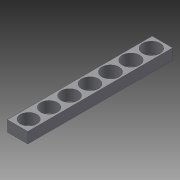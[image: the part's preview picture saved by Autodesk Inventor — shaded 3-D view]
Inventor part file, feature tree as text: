
AUTODESK INVENTOR PART (.ipt)
format: ipt  version: 2015 (Build 190159000, 159)  size: 107,008 bytes
history: native  units: in
note: dims shown in document units (in); Inventor stores cm internally (conversion verified against a paired STEP export)
features: extrude x2, sketch x2
ambient origin geometry x8: Origin, YZ Plane, XZ Plane, XY Plane, X Axis, Y Axis, Z Axis, Center Point
bodies: Solid1 (feature_tree)
feature tree (4):
  extrude  "Extrusion1"  Depth=3.3465in
  extrude  "Extrusion2"  Depth=0.4724in
  sketch  "Sketch1"  dims[d6=0.4724in d7=3.3465in]
  sketch  "Sketch2"  dims[d8=0.25in d9=0.0in d10=0.3819in d11=0.3858in d12=0.3898in d13=0.3937in d14=0.3976in d15=0.4016in d16=0.4724in d17=0.4724in d18=0.4724in d19=0.4724in d20=0.4724in d21=0.4055in d22=0.4724in d23=0.0in d24=0.0in]
